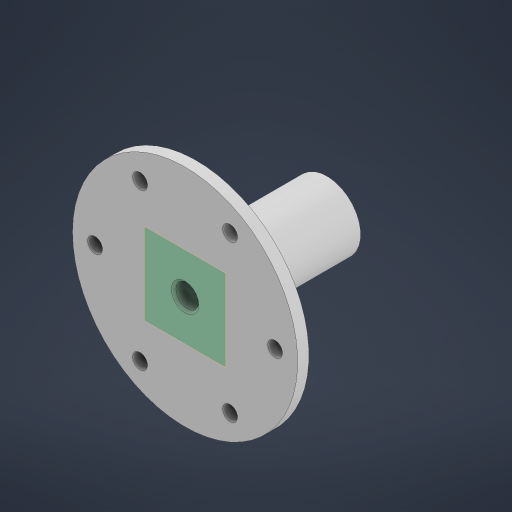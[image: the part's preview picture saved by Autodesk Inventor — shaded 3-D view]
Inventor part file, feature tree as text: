
AUTODESK INVENTOR PART (.ipt)
format: ipt  version: 2024.1 (Build 281209000, 209)  size: 239,104 bytes
history: native  units: in
note: dims shown in document units (in); Inventor stores cm internally (conversion verified against a paired STEP export)
features: extrude x6, other x5, sketch x4, reference x3, chamfer x2, plane x1
ambient origin geometry x8: Origin, YZ Plane, XZ Plane, XY Plane, X Axis, Y Axis, Z Axis, Center Point
bodies: Solid1 (feature_tree)
feature tree (21):
  extrude  "Extrusion1"  Depth=0.003in
  plane  "Work Plane1"
  sketch  "Sketch2"  dims[d2=0.5906in d3=2.2444in d4=0.0in d5=0.0in d6=5.4134in]
  extrude  "Extrusion2"  Depth=5.4134in
  extrude  "Extrusion3"  Depth=1.0in
  extrude  "Extrusion4"  Depth=0.125in
  extrude  "Extrusion5"  Depth=0.125in
  extrude  "Extrusion6"  Depth=1.0in
  chamfer  "Chamfer2"  Distance=2.3622in Angle=360.0deg
  chamfer  "Chamfer1"  Distance=1.0in
  sketch  "Sketch1"  dims[d0=0.002in d1=0.003in]
  reference  "Reference1"
  reference  "Reference2"
  sketch  "Sketch3"  dims[d7=21.6535in d8=1.0in]
  sketch  "Sketch4"  dims[d9=2.5in d10=24.0in d11=0.1654in d12=1.0in d13=2.3622in d15=360.0deg d17=1.0in d18=1.0in d19=0.75in d20=1.5748in d21=0.0in d22=0.4in d23=0.0in d24=0.125in d25=0.0in d26=0.35in d27=0.125in d28=45.0deg d29=1.2601in d30=0.0in d31=0.002in d32=1.5748in d33=0.0in d34=0.025in d35=0.125in d36=45.0deg]
  reference  "Reference3"
  other  "<userpath>\Documents\School\FallCAD\Trebuchet\Trebuchet.iam"
  other  "Trebuchet.iam"
  other  "BallBearing_8x22x7mm:1"
  other  "AcrylicRod:1"
  other  "Assembly1"
